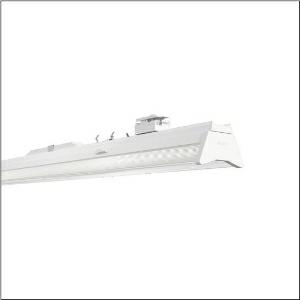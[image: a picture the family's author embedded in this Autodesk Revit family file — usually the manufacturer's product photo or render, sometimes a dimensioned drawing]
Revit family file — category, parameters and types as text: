
# Revit family: licross_r__21_performance_mo_52td16dn4a5g_459a
name_source: partatom
category: Lighting Fixtures
units: mm (PartAtom-declared; Revit-internal decimal feet)

## family parameters
Cut with Voids When Loaded = No
Host = Face
Light Source = No
Part Type = Normal
Room Calculation Point = No
Round Connector Dimension = Use Diameter
Shared = No

## types (1)
- --- (1 x LED, 10840 lm, 62 W, 4000K)
    Apparent Load = 62 VA
    CIE Flux Codes = 66 88 96 79 100
    Color Rendering = 80
    Color Temperature = 4000K
    Default Elevation = 1800 mm
    Description = Licross® 21 Performance MO, luminaire insert, of sheet steel, galvanised, coil coated, white, length: 1.500mm, width: 120mm, height: 123mm, LED rated luminous flux: 10.840lm, light colour: 840, control gear: DALI 2, with plug, 5-pole, with phase selection, mains connection: 220..240V, AC, 50/60Hz, rated input power: 62W, internal wiring halogen-free, primary light control with lens, of plastic, primary optical cover: cover, of PMMA, light emission: direct/indirect distribution, primary light characteristic: symmetric, protection rating (complete): IP54, insulation class (complete): insulation class I (protective earthing), certification: CE, ENEC, VDE, UKCA, protection symbol: D if used in an environment with non-conductive dust loads with corresponding accessories, impact resistance: IK06, permissible ambient temperature for indoor applications: -25..+35°C, corresponds to IFS (International Featured Standards) requirements for safety and quality in the food industry, reducing of maximum allowable ambient temperature of 5°C with ceiling mounting, LABS conformity tested according to VDMA 24364:2018-05, packaging unit: 1 piece
    Height = 114 mm
    Lamp = 1 x LED
    Lamp Light Flux = 10840 lm
    Lamp Power = 62 W
    Lamp count = 1
    Length = 1500 mm
    Luminous efficacy = 175 lm/W
    Manufacturer = Siteco
    ModVariant = No
    Model = 52TD16DN4A5G
    Mounting Place = Ceiling
    Mounting Type = Pendant
    Number of Poles = 1
    OnlyDefault = Yes
    Power Factor = 1
    Product Name = Licross® 21 Performance MO
    Product group = luminaire insert | ceiling pendant
    ProductGroupID = 902
    Protection Class = Protection class I
    Protection Degree = IP 54
    RLX_Detail_Level = 1
    RLX_Emergency_Light_Flux = 0 lm
    RLX_Emergency_Type = 0
    RLX_Emergency_Type_DB = No
    RlxData = <blob elided: 34181 chars, md5=67b6df45>
    Socket = socket
    Standby Power = 0 W
    System Light Flux = 10840 lm
    System Power = 62 W
    Type Comments = factory setting: luminous flux: 100 % | dim-lin: 254 | 418 mA
    Type Image = l_1256138.jpg
    URL = http://relux.com
    VarID = @adj_150667
    Voltage = 0 V
    Weight = 0.00 kg
    Width = 120 mm

## geometry (parser evidence)
native form markers: Blend x4, Sweep x11
no freeform markers — native parametric forms only
